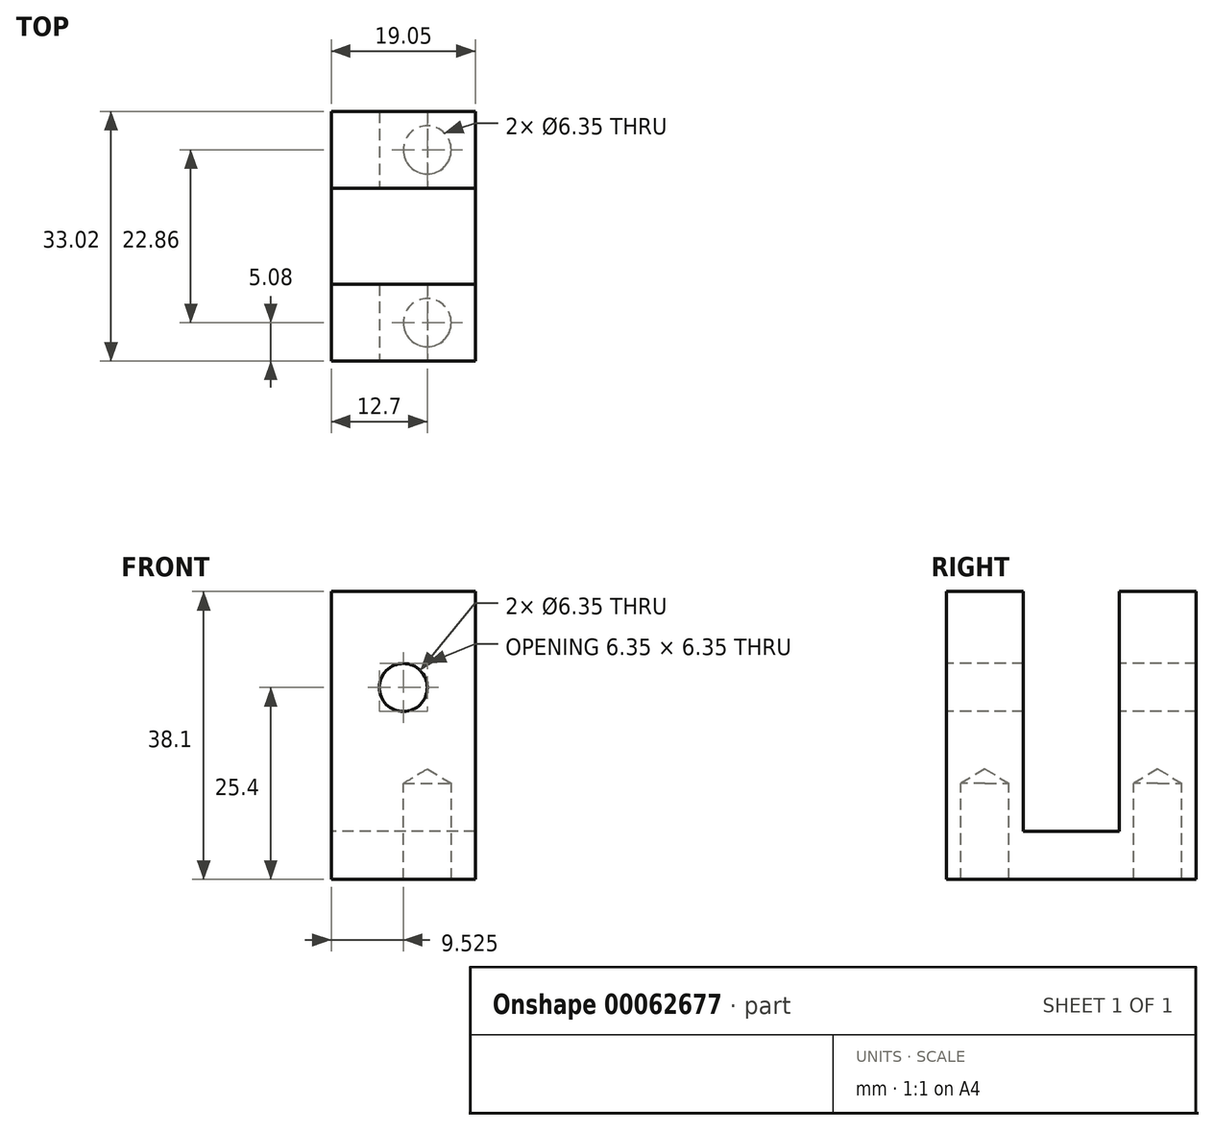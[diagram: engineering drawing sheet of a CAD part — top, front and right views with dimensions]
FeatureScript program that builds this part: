
annotation { "Feature Type Name" : "Feature", "Feature Type Description" : "" }
export const myFeature = defineFeature(function(context is Context, id is Id, definition is map)
    precondition{}
    {
        {
            var Q0;
            Q0=qCreatedBy(makeId("Right.planeOp"),FACE);
            var sketch = newSketch(context, id + "F0", { "sketchPlane" : qUnion([Q0])});
            skLineSegment(sketch, "E0.bottom", {"start": v(0, 0) * mm, "end": v(33.02, 0) * mm});
            skLineSegment(sketch, "E0.top", {"start": v(0, 38.1) * mm, "end": v(10.16, 38.1) * mm});
            skLineSegment(sketch, "E0.left", {"start": v(0, 0) * mm, "end": v(0, 38.1) * mm});
            skLineSegment(sketch, "E0.right", {"start": v(33.02, 0) * mm, "end": v(33.02, 38.1) * mm});
            skLineSegment(sketch, "E1.top", {"start": v(10.16, 6.35) * mm, "end": v(22.86, 6.35) * mm});
            skLineSegment(sketch, "E1.left", {"start": v(10.16, 38.1) * mm, "end": v(10.16, 6.35) * mm});
            skLineSegment(sketch, "E1.right", {"start": v(22.86, 38.1) * mm, "end": v(22.86, 6.35) * mm});
            skLineSegment(sketch, "E2.trimOffspring", {"start": v(22.86, 38.1) * mm, "end": v(33.02, 38.1) * mm});
            skSolve(sketch);
        }
        {
            var Q0;
            Q0=makeQuery(id+"F0.imprint","IMPRINT",FACE,{"disambiguationData":[TD([[makeQuery(id+"F0.imprint","IMPRINT",EDGE,{"derivedFrom":sQuery(id+"F0.wireOp",EDGE,"E0.bottom")}),1.0]])]});
            extrude(context, id + "F1", {"entities" : qUnion([Q0]), "depth" : 19.05 * mm});
        }
        {
            var Q0;
            Q0=makeQuery(id+"F1.opExtrude","SWEPT_FACE",FACE,{"disambiguationData":[OSD([sQuery(id+"F0.wireOp",EDGE,"E0.right")])]});
            var sketch = newSketch(context, id + "F2", { "sketchPlane" : qUnion([Q0])});
            skCircle(sketch, "E3", {"center": v(-9.53, 25.4) * mm, "radius": 3.18 * mm});
            skSolve(sketch);
        }
        {
            var Q0;
            Q0=sQuery(id+"F2.wireOp",VERTEX,"E3.center");
            var Q1;
            Q1=makeQuery(id+"F1.opExtrude","SWEPT_BODY",BODY,{"disambiguationData":[OSD([sQuery(id+"F0.wireOp",EDGE,"E0.bottom"),sQuery(id+"F0.wireOp",EDGE,"E0.top"),sQuery(id+"F0.wireOp",EDGE,"E0.left"),sQuery(id+"F0.wireOp",EDGE,"E0.right"),sQuery(id+"F0.wireOp",EDGE,"E1.top"),sQuery(id+"F0.wireOp",EDGE,"E1.left"),sQuery(id+"F0.wireOp",EDGE,"E1.right"),sQuery(id+"F0.wireOp",EDGE,"E2.trimOffspring")])]});
            hole(context, id + "F3", {"style" : HoleStyle.SIMPLE, "holeDiameter" : 6.35 * mm, "endStyle" : HoleEndStyle.THROUGH, "locations" : qUnion([Q0]), "scope" : qUnion([Q1])});
        }
        {
            var Q0;
            Q0=makeQuery(id+"F1.opExtrude","SWEPT_FACE",FACE,{"disambiguationData":[OSD([sQuery(id+"F0.wireOp",EDGE,"E0.bottom")])]});
            var sketch = newSketch(context, id + "F4", { "sketchPlane" : qUnion([Q0])});
            skCircle(sketch, "E4", {"center": v(12.7, -5.08) * mm, "radius": 3.18 * mm});
            skCircle(sketch, "E5", {"center": v(12.7, -27.94) * mm, "radius": 3.18 * mm});
            skSolve(sketch);
        }
        {
            var Q0;
            Q0=sQuery(id+"F4.wireOp",VERTEX,"E4.center");
            var Q1;
            Q1=sQuery(id+"F4.wireOp",VERTEX,"E5.center");
            var Q2;
            Q2=makeQuery(id+"F1.opExtrude","SWEPT_BODY",BODY,{"disambiguationData":[OSD([sQuery(id+"F0.wireOp",EDGE,"E0.bottom"),sQuery(id+"F0.wireOp",EDGE,"E0.top"),sQuery(id+"F0.wireOp",EDGE,"E0.left"),sQuery(id+"F0.wireOp",EDGE,"E0.right"),sQuery(id+"F0.wireOp",EDGE,"E1.top"),sQuery(id+"F0.wireOp",EDGE,"E1.left"),sQuery(id+"F0.wireOp",EDGE,"E1.right"),sQuery(id+"F0.wireOp",EDGE,"E2.trimOffspring")])]});
            hole(context, id + "F5", {"style" : HoleStyle.SIMPLE, "holeDiameter" : 6.35 * mm, "endStyle" : HoleEndStyle.BLIND, "holeDepth" : 12.7 * mm, "locations" : qUnion([Q0, Q1]), "scope" : qUnion([Q2])});
        }
    });
